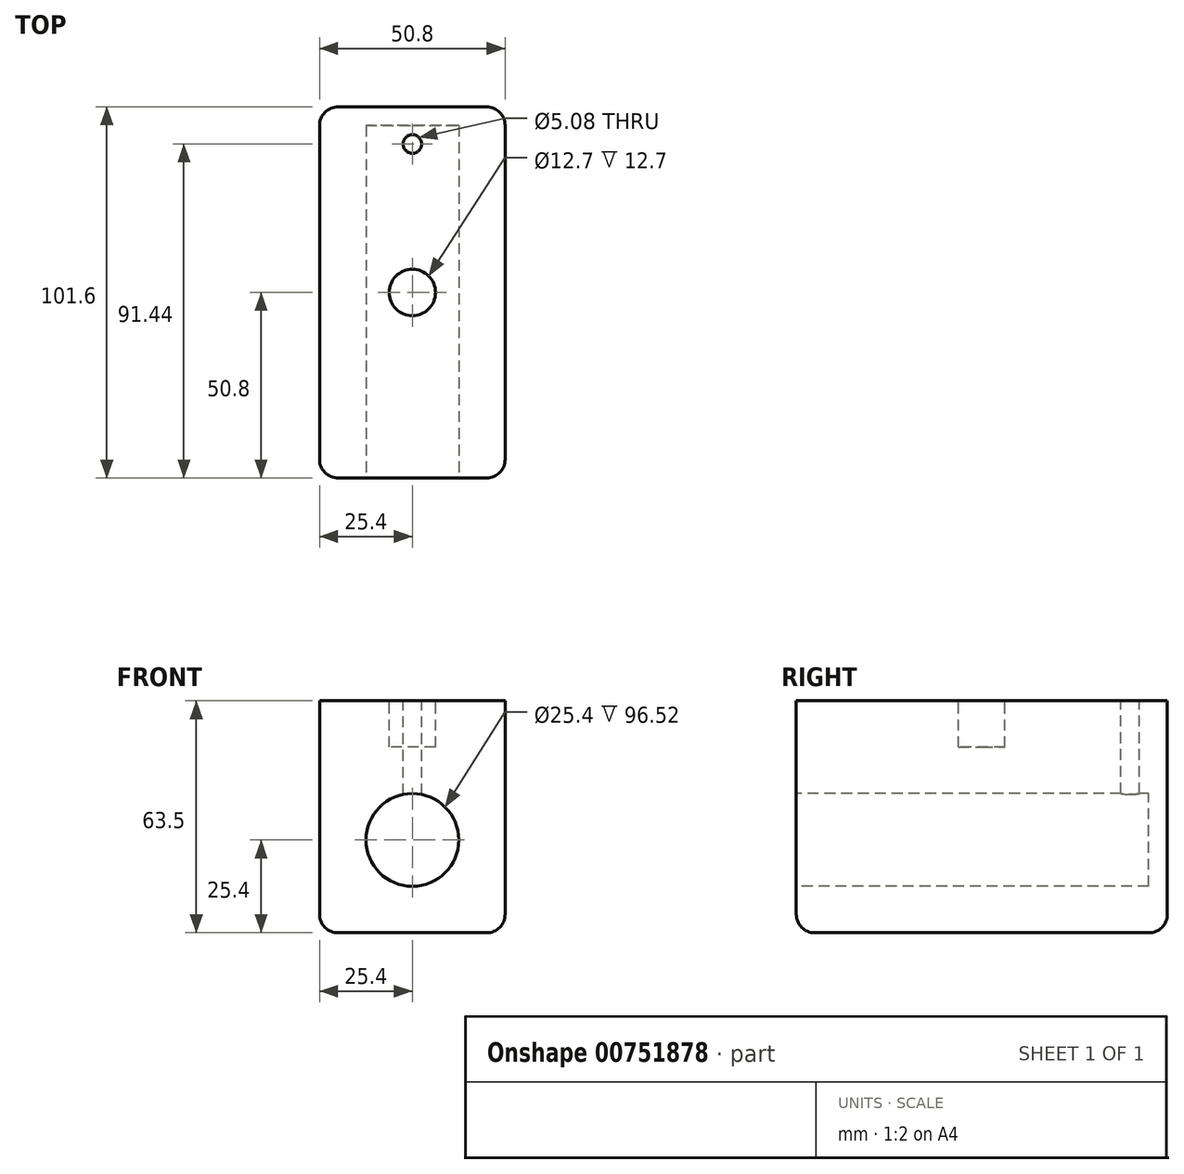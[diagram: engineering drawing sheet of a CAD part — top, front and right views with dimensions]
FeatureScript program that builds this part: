
annotation { "Feature Type Name" : "Feature", "Feature Type Description" : "" }
export const myFeature = defineFeature(function(context is Context, id is Id, definition is map)
    precondition{}
    {
        {
            var Q0;
            Q0=qCreatedBy(makeId("Top.planeOp"),FACE);
            var sketch = newSketch(context, id + "F0", { "sketchPlane" : qUnion([Q0])});
            skLineSegment(sketch, "E0.bottom", {"start": v(-25.4, 50.8) * mm, "end": v(25.4, 50.8) * mm});
            skLineSegment(sketch, "E0.top", {"start": v(-25.4, -50.8) * mm, "end": v(25.4, -50.8) * mm});
            skLineSegment(sketch, "E0.left", {"start": v(-25.4, 50.8) * mm, "end": v(-25.4, -50.8) * mm});
            skLineSegment(sketch, "E0.right", {"start": v(25.4, 50.8) * mm, "end": v(25.4, -50.8) * mm});
            skPoint(sketch, "E0.middle", {"position": v(0, 0) * mm});
            skSolve(sketch);
        }
        {
            var Q0;
            Q0=makeQuery(id+"F0.imprint","IMPRINT",FACE,{"disambiguationData":[TD([[makeQuery(id+"F0.imprint","IMPRINT",EDGE,{"derivedFrom":sQuery(id+"F0.wireOp",EDGE,"E0.bottom")}),-1.0]])]});
            extrude(context, id + "F1", {"entities" : qUnion([Q0]), "depth" : 63.5 * mm, "offsetDistance" : 25.4 * mm});
        }
        {
            var Q0;
            Q0=makeQuery(id+"F1.opExtrude","SWEPT_FACE",FACE,{"disambiguationData":[OSD([sQuery(id+"F0.wireOp",EDGE,"E0.top")])]});
            var sketch = newSketch(context, id + "F2", { "sketchPlane" : qUnion([Q0])});
            skCircle(sketch, "E1", {"center": v(0, 25.4) * mm, "radius": 12.7 * mm});
            skSolve(sketch);
        }
        {
            var Q0;
            Q0=makeQuery(id+"F2.imprint","IMPRINT",FACE,{"disambiguationData":[TD([[makeQuery(id+"F2.imprint","IMPRINT",EDGE,{"derivedFrom":sQuery(id+"F2.wireOp",EDGE,"E1")}),1.0]])]});
            extrude(context, id + "F3", {"entities" : qUnion([Q0]), "operationType" : NewBodyOperationType.REMOVE, "oppositeDirection" : true, "depth" : 96.52 * mm, "offsetDistance" : 25.4 * mm});
        }
        {
            var Q0;
            Q0=makeQuery(id+"F1.opExtrude","CAP_FACE",FACE,{"disambiguationData":[OSD([sQuery(id+"F0.wireOp",EDGE,"E0.bottom"),sQuery(id+"F0.wireOp",EDGE,"E0.top"),sQuery(id+"F0.wireOp",EDGE,"E0.left"),sQuery(id+"F0.wireOp",EDGE,"E0.right")])],"isStart":false});
            var sketch = newSketch(context, id + "F4", { "sketchPlane" : qUnion([Q0])});
            skCircle(sketch, "E2", {"center": v(0, 40.64) * mm, "radius": 2.54 * mm});
            skSolve(sketch);
        }
        {
            var Q0;
            Q0=makeQuery(id+"F4.imprint","IMPRINT",FACE,{"disambiguationData":[TD([[makeQuery(id+"F4.imprint","IMPRINT",EDGE,{"derivedFrom":sQuery(id+"F4.wireOp",EDGE,"E2")}),1.0]])]});
            extrude(context, id + "F5", {"entities" : qUnion([Q0]), "operationType" : NewBodyOperationType.REMOVE, "oppositeDirection" : true, "depth" : 36.32 * mm, "offsetDistance" : 25.4 * mm});
        }
        {
            var Q0;
            Q0=makeQuery(id+"F1.opExtrude","CAP_FACE",FACE,{"disambiguationData":[OSD([sQuery(id+"F0.wireOp",EDGE,"E0.bottom"),sQuery(id+"F0.wireOp",EDGE,"E0.top"),sQuery(id+"F0.wireOp",EDGE,"E0.left"),sQuery(id+"F0.wireOp",EDGE,"E0.right")])],"isStart":false});
            var sketch = newSketch(context, id + "F6", { "sketchPlane" : qUnion([Q0])});
            skCircle(sketch, "E3", {"center": v(0, 0) * mm, "radius": 6.35 * mm});
            skSolve(sketch);
        }
        {
            var Q0;
            Q0=makeQuery(id+"F6.imprint","IMPRINT",FACE,{"disambiguationData":[TD([[makeQuery(id+"F6.imprint","IMPRINT",EDGE,{"derivedFrom":sQuery(id+"F6.wireOp",EDGE,"E3")}),1.0]])]});
            extrude(context, id + "F7", {"entities" : qUnion([Q0]), "operationType" : NewBodyOperationType.REMOVE, "oppositeDirection" : true, "depth" : 12.7 * mm, "offsetDistance" : 25.4 * mm});
        }
        {
            var Q0;
            Q0=makeQuery(id+"F1.opExtrude","SWEPT_EDGE",EDGE,{"disambiguationData":[OSD([sQuery(id+"F0.wireOp",EDGE,"E0.top"),sQuery(id+"F0.wireOp",EDGE,"E0.right")])]});
            var Q1;
            Q1=makeQuery(id+"F1.opExtrude","SWEPT_EDGE",EDGE,{"disambiguationData":[OSD([sQuery(id+"F0.wireOp",EDGE,"E0.top"),sQuery(id+"F0.wireOp",EDGE,"E0.left")])]});
            var Q2;
            Q2=makeQuery(id+"F1.opExtrude","SWEPT_EDGE",EDGE,{"disambiguationData":[OSD([sQuery(id+"F0.wireOp",EDGE,"E0.bottom"),sQuery(id+"F0.wireOp",EDGE,"E0.left")])]});
            var Q3;
            Q3=makeQuery(id+"F1.opExtrude","CAP_EDGE",EDGE,{"disambiguationData":[OSD([sQuery(id+"F0.wireOp",EDGE,"E0.left")])],"isStart":true});
            var Q4;
            Q4=makeQuery(id+"F1.opExtrude","CAP_EDGE",EDGE,{"disambiguationData":[OSD([sQuery(id+"F0.wireOp",EDGE,"E0.bottom")])],"isStart":true});
            var Q5;
            Q5=makeQuery(id+"F1.opExtrude","SWEPT_EDGE",EDGE,{"disambiguationData":[OSD([sQuery(id+"F0.wireOp",EDGE,"E0.bottom"),sQuery(id+"F0.wireOp",EDGE,"E0.right")])]});
            var Q6;
            Q6=makeQuery(id+"F1.opExtrude","CAP_EDGE",EDGE,{"disambiguationData":[OSD([sQuery(id+"F0.wireOp",EDGE,"E0.right")])],"isStart":true});
            var Q7;
            Q7=makeQuery(id+"F1.opExtrude","CAP_EDGE",EDGE,{"disambiguationData":[OSD([sQuery(id+"F0.wireOp",EDGE,"E0.top")])],"isStart":true});
            fillet(context, id + "F8", {"entities" : qUnion([Q0, Q1, Q2, Q3, Q4, Q5, Q6, Q7]), "radius" : 5.08 * mm, "tangentPropagation" : true, "allowEdgeOverflow" : false});
        }
    });
